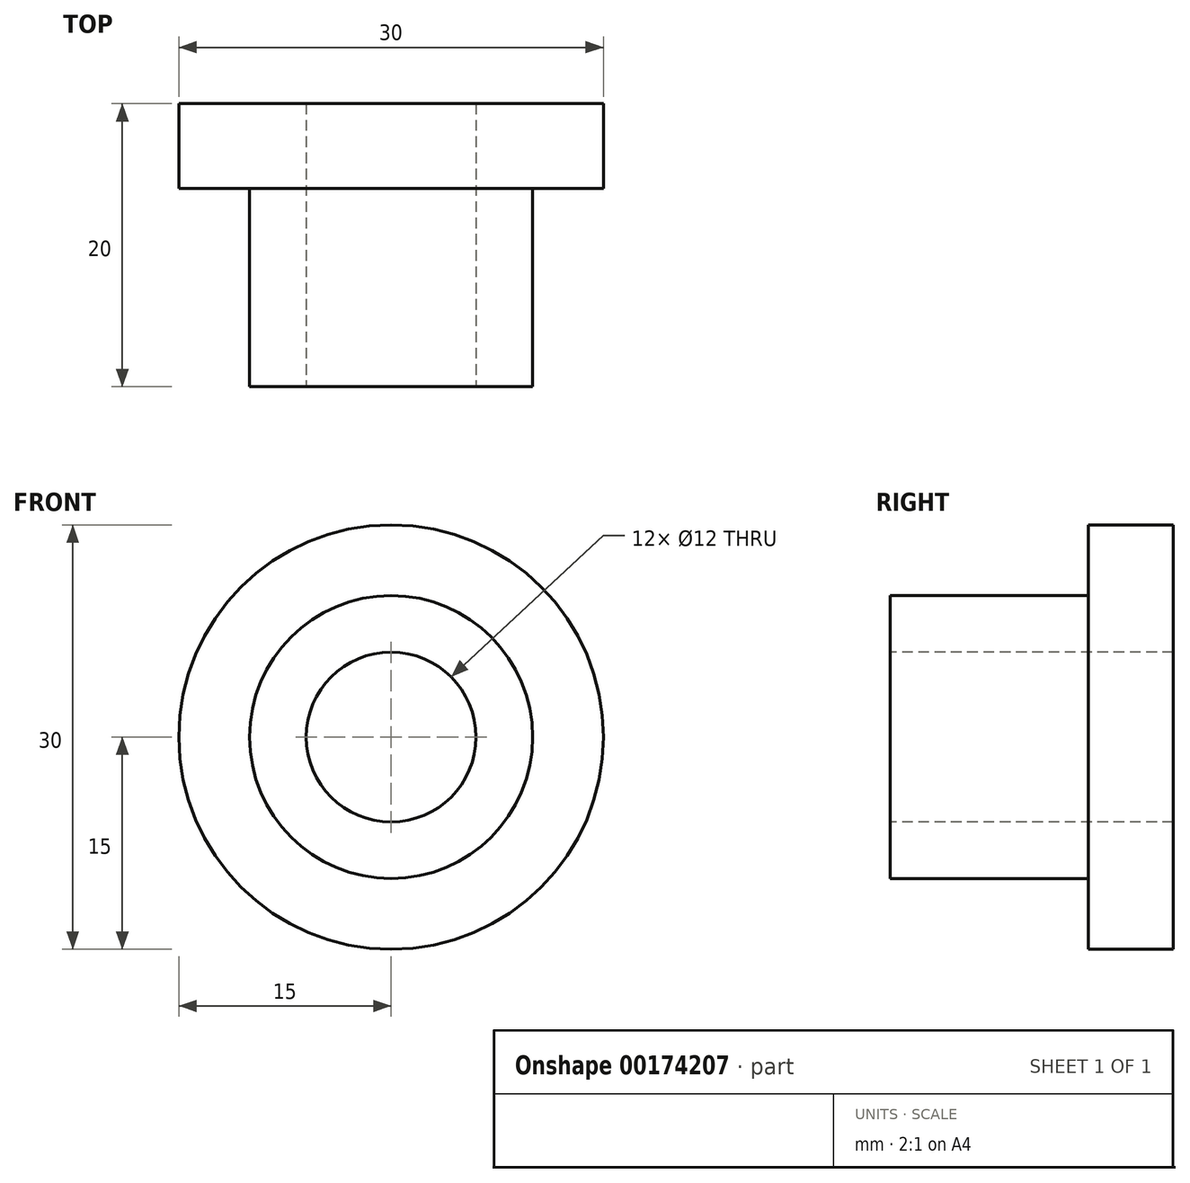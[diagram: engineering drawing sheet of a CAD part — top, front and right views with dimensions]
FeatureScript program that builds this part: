
annotation { "Feature Type Name" : "Feature", "Feature Type Description" : "" }
export const myFeature = defineFeature(function(context is Context, id is Id, definition is map)
    precondition{}
    {
        {
            var Q0;
            Q0=qCreatedBy(makeId("Right.planeOp"),FACE);
            var sketch = newSketch(context, id + "F0", { "sketchPlane" : qUnion([Q0])});
            skLineSegment(sketch, "E0", {"start": v(0, 0) * mm, "end": v(20, 0) * mm, "construction": true});
            skLineSegment(sketch, "E1", {"start": v(20, -6) * mm, "end": v(0, -6) * mm});
            skLineSegment(sketch, "E2", {"start": v(0, -6) * mm, "end": v(0, -10) * mm});
            skLineSegment(sketch, "E3", {"start": v(0, -10) * mm, "end": v(14, -10) * mm});
            skLineSegment(sketch, "E4", {"start": v(14, -10) * mm, "end": v(14, -15) * mm});
            skLineSegment(sketch, "E5", {"start": v(14, -15) * mm, "end": v(20, -15) * mm});
            skLineSegment(sketch, "E6", {"start": v(20, -15) * mm, "end": v(20, -6) * mm});
            skSolve(sketch);
        }
        {
            var Q0;
            Q0 = qSketchRegion(id + "F0", true);
            var Q1;
            Q1=sQuery(id+"F0.wireOp",EDGE,"E0");
            revolve(context, id + "F1", {"entities" : qUnion([Q0]), "axis" : qUnion([Q1]), "revolveType" : RevolveType.FULL});
        }
    });
